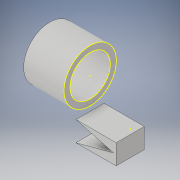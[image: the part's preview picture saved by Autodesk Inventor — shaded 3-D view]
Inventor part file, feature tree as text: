
AUTODESK INVENTOR PART (.ipt)
format: ipt  version: 2019 (Build 230136000, 136)  size: 133,120 bytes
history: native  units: mm
features: sketch x9, extrude x2, revolve x1
ambient origin geometry x8: Origin, YZ Plane, XZ Plane, XY Plane, X Axis, Y Axis, Z Axis, Center Point
bodies: Solid1 (feature_tree)
feature tree (12):
  revolve  "Revolution1"  [1 undecoded]
  sketch  "Sketch2"  dims[d3=10.0mm d4=20.0mm]
  sketch  "Sketch3"  dims[d5=20.0mm d6=90.0deg]
  sketch  "Sketch4"  dims[d20=10.0mm]
  sketch  "Sketch5"  dims[d21=14.0mm]
  extrude  "Extrusion1"  Depth=20.0mm
  extrude  "Extrusion2"  TaperAngle=90.0deg  [1 undecoded]
  sketch  "Sketch8"  dims[d25=15.0deg]
  sketch  "Sketch9"  dims[d26=14.0mm d27=0.0mm]
  sketch  "Sketch1"  dims[d1=3.0mm d2=20.0mm]
  sketch  "Sketch6"  dims[d22=20.0mm d23=0.0mm]
  sketch  "Sketch7"  dims[d24=15.0deg]
note: 2 required parameter values undecoded (feature->parameter linkage not recoverable at this tier; creation-order binding heuristic only, values carry confidence <= 0.55)